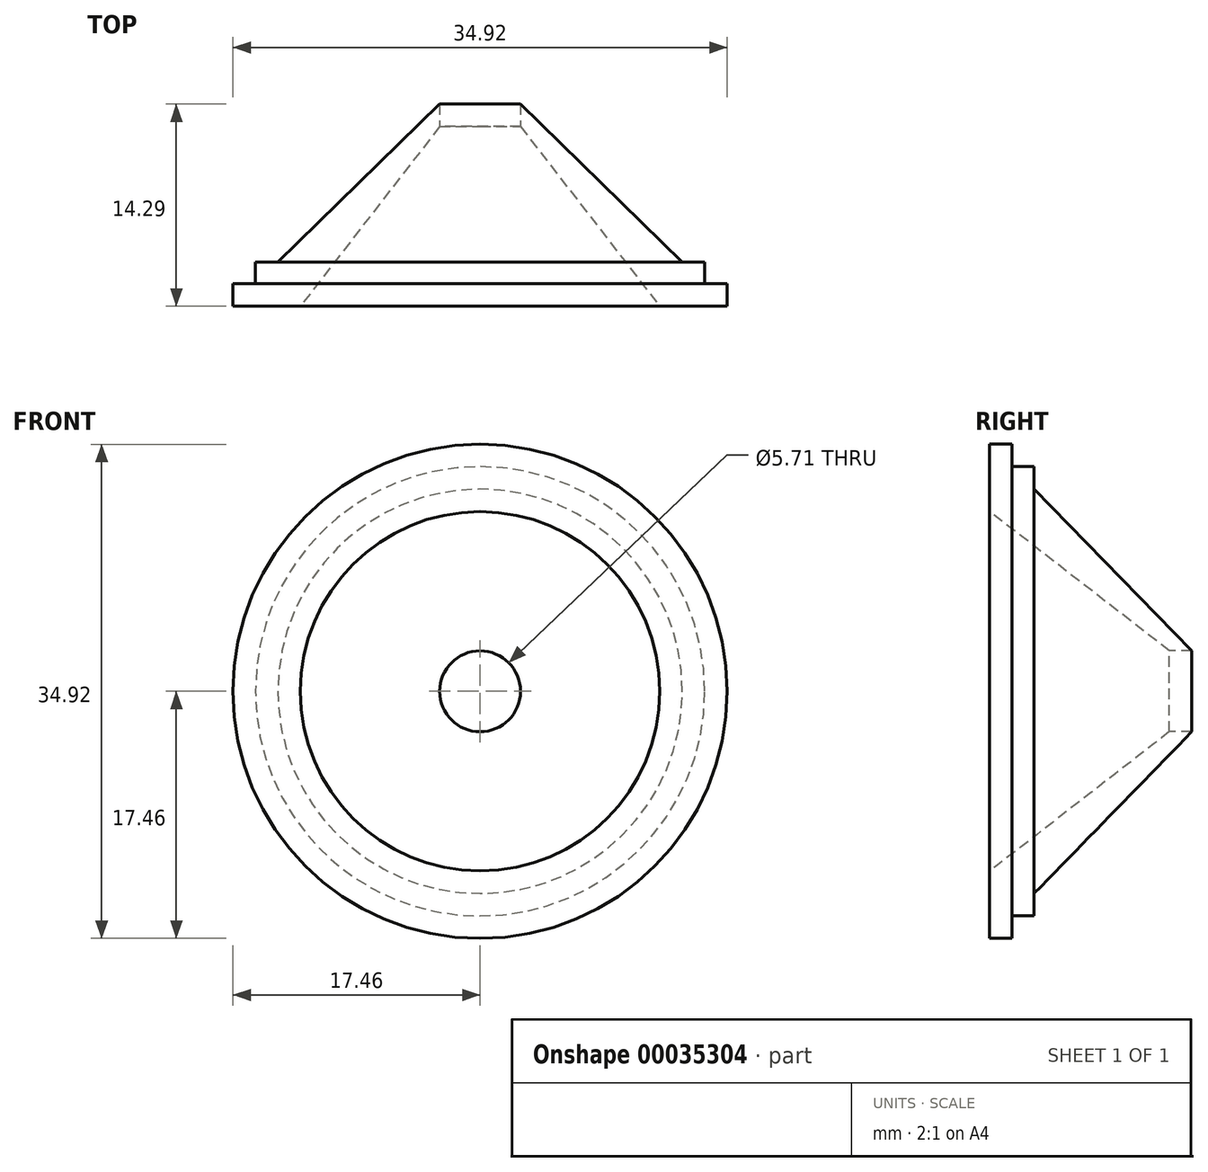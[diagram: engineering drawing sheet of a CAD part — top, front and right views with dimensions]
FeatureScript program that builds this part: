
annotation { "Feature Type Name" : "Feature", "Feature Type Description" : "" }
export const myFeature = defineFeature(function(context is Context, id is Id, definition is map)
    precondition{}
    {
        {
            var Q0;
            Q0=qCreatedBy(makeId("Right.planeOp"),FACE);
            var sketch = newSketch(context, id + "F0", { "sketchPlane" : qUnion([Q0])});
            skLineSegment(sketch, "E0", {"start": v(51.08, 0) * mm, "end": v(78, 0) * mm, "construction": true});
            skLineSegment(sketch, "E1", {"start": v(-13.87, 15.88) * mm, "end": v(-13.87, 17.46) * mm});
            skLineSegment(sketch, "E2", {"start": v(-15.46, 12.7) * mm, "end": v(-2.76, 2.86) * mm});
            skLineSegment(sketch, "E3", {"start": v(-2.76, 2.86) * mm, "end": v(-1.17, 2.86) * mm});
            skPoint(sketch, "E4", {"position": v(-1.96, 2.86) * mm});
            skLineSegment(sketch, "E5", {"start": v(-15.46, 12.7) * mm, "end": v(-15.46, 17.46) * mm});
            skLineSegment(sketch, "E6", {"start": v(-15.46, 17.46) * mm, "end": v(-13.87, 17.46) * mm});
            skLineSegment(sketch, "E7", {"start": v(-13.87, 15.88) * mm, "end": v(-12.32, 15.88) * mm});
            skLineSegment(sketch, "E8", {"start": v(-12.32, 15.88) * mm, "end": v(-12.32, 14.29) * mm});
            skLineSegment(sketch, "E9", {"start": v(-12.32, 14.29) * mm, "end": v(-1.17, 2.86) * mm});
            skSolve(sketch);
        }
        {
            var Q0;
            Q0=makeQuery(id+"F0.imprint","IMPRINT",FACE,{"disambiguationData":[TD([[makeQuery(id+"F0.imprint","IMPRINT",EDGE,{"derivedFrom":sQuery(id+"F0.wireOp",EDGE,"E1")}),1.0]])]});
            var Q1;
            Q1=sQuery(id+"F0.wireOp",EDGE,"E0");
            revolve(context, id + "F1", {"entities" : qUnion([Q0]), "axis" : qUnion([Q1]), "revolveType" : RevolveType.FULL});
        }
    });
